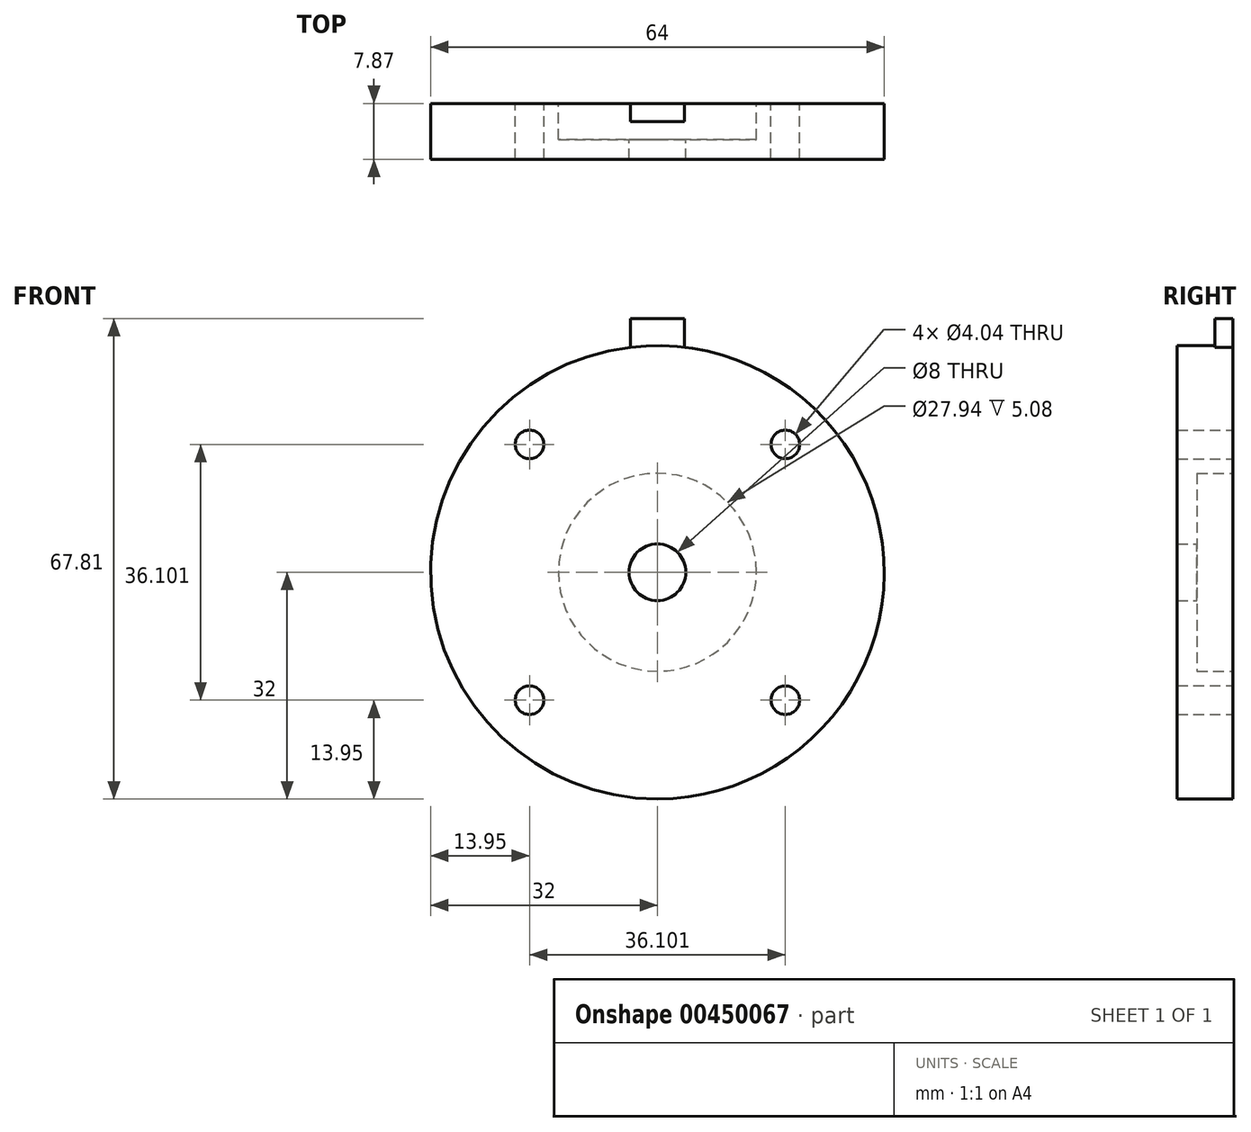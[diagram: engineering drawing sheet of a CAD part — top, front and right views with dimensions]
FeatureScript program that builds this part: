
annotation { "Feature Type Name" : "Feature", "Feature Type Description" : "" }
export const myFeature = defineFeature(function(context is Context, id is Id, definition is map)
    precondition{}
    {
        {
            var Q0;
            Q0=qCreatedBy(makeId("Front.planeOp"),FACE);
            var sketch = newSketch(context, id + "F0", { "sketchPlane" : qUnion([Q0])});
            skCircle(sketch, "E0", {"center": v(0, 0) * mm, "radius": 32 * mm});
            skCircle(sketch, "E1", {"center": v(0, 0) * mm, "radius": 4 * mm});
            skLineSegment(sketch, "E2", {"start": v(-22.63, 22.63) * mm, "end": v(-19.48, 19.48) * mm, "construction": true});
            skLineSegment(sketch, "E3", {"start": v(22.63, 22.63) * mm, "end": v(19.48, 19.48) * mm, "construction": true});
            skCircle(sketch, "E4", {"center": v(-18.05, 18.05) * mm, "radius": 2.02 * mm});
            skArc(sketch, "E5", {"start": v(19.48, 19.48) * mm, "mid": v(16.62, 19.48) * mm, "end": v(16.62, 16.62) * mm});
            skArc(sketch, "E6", {"start": v(16.62, 16.62) * mm, "mid": v(19.48, 16.62) * mm, "end": v(19.48, 19.48) * mm});
            skArc(sketch, "E7", {"start": v(16.62, -16.62) * mm, "mid": v(16.62, -19.48) * mm, "end": v(19.48, -19.48) * mm});
            skArc(sketch, "E8", {"start": v(19.48, -19.48) * mm, "mid": v(19.48, -16.62) * mm, "end": v(16.62, -16.62) * mm});
            skLineSegment(sketch, "E9", {"start": v(-16.62, -16.62) * mm, "end": v(-16.62, -16.62) * mm});
            skArc(sketch, "E10", {"start": v(-19.48, -19.48) * mm, "mid": v(-16.62, -19.48) * mm, "end": v(-16.62, -16.62) * mm});
            skArc(sketch, "E11", {"start": v(-16.62, -16.62) * mm, "mid": v(-19.48, -16.62) * mm, "end": v(-19.48, -19.48) * mm});
            skLineSegment(sketch, "E12", {"start": v(19.48, -19.48) * mm, "end": v(22.63, -22.63) * mm, "construction": true});
            skLineSegment(sketch, "E13", {"start": v(-19.48, -19.48) * mm, "end": v(-22.63, -22.63) * mm, "construction": true});
            skSolve(sketch);
        }
        {
            var Q0;
            Q0=makeQuery(id+"F0.imprint","IMPRINT",FACE,{"disambiguationData":[TD([[makeQuery(id+"F0.imprint","IMPRINT",EDGE,{"derivedFrom":sQuery(id+"F0.wireOp",EDGE,"E0")}),1.0]])]});
            extrude(context, id + "F1", {"entities" : qUnion([Q0]), "depth" : 7.87 * mm});
        }
        {
            var Q0;
            Q0=qCreatedBy(makeId("Top.planeOp"),FACE);
            cPlane(context, id + "F2", {"entities" : qUnion([Q0]), "cplaneType" : CPlaneType.OFFSET, "offset" : 32 * mm, "width" : 152.4 * mm, "height" : 152.4 * mm});
        }
        {
            var Q0;
            Q0=qCreatedBy(id+"F2.planeOp",FACE);
            var sketch = newSketch(context, id + "F3", { "sketchPlane" : qUnion([Q0])});
            skLineSegment(sketch, "E14.0", {"start": v(32, 0) * mm, "end": v(-32, 0) * mm});
            skLineSegment(sketch, "E15", {"start": v(-3.81, 0) * mm, "end": v(-3.8, -2.54) * mm});
            skLineSegment(sketch, "E16", {"start": v(-3.8, -2.54) * mm, "end": v(3.8, -2.54) * mm});
            skLineSegment(sketch, "E17", {"start": v(3.81, -2.54) * mm, "end": v(3.8, 0) * mm});
            skPoint(sketch, "E18", {"position": v(0, -2.54) * mm});
            skSolve(sketch);
        }
        {
            var Q0;
            {var subQ0=sQuery(id+"F3.wireOp",EDGE,"E15");Q0=makeQuery(id+"F3.imprint","IMPRINT",FACE,{"disambiguationData":[TD([[makeQuery(id+"F3.imprint","IMPRINT",EDGE,{"derivedFrom":subQ0}),1.0]])]});}
            var Q1;
            Q1=makeQuery(id+"F1.opExtrude","SWEPT_FACE",FACE,{"disambiguationData":[OSD([sQuery(id+"F0.wireOp",EDGE,"E0")])]});
            extrude(context, id + "F4", {"entities" : qUnion([Q0]), "operationType" : NewBodyOperationType.ADD, "depth" : 3.8 * mm, "hasSecondDirection" : true, "secondDirectionBound" : BoundingType.UP_TO_SURFACE, "secondDirectionOppositeDirection" : true, "secondDirectionBoundEntityFace" : qUnion([Q1]), "secondDirectionDepth" : 25.4 * mm});
        }
        {
            var Q0;
            Q0=makeQuery(id+"F4.boolean.opBoolean","MERGE",FACE,{"derivedFrom":[makeQuery(id+"F1.opExtrude","CAP_FACE",FACE,{"disambiguationData":[OSD([sQuery(id+"F0.wireOp",EDGE,"E0"),sQuery(id+"F0.wireOp",EDGE,"E1"),sQuery(id+"F0.wireOp",EDGE,"E4"),sQuery(id+"F0.wireOp",EDGE,"E5"),sQuery(id+"F0.wireOp",EDGE,"E6"),sQuery(id+"F0.wireOp",EDGE,"E7"),sQuery(id+"F0.wireOp",EDGE,"E8"),sQuery(id+"F0.wireOp",EDGE,"E10"),sQuery(id+"F0.wireOp",EDGE,"E11")])],"isStart":true}),makeQuery(id+"F4.opExtrude","SWEPT_FACE",FACE,{"disambiguationData":[OSD([sQuery(id+"F3.wireOp",EDGE,"E14.0")])]})]});
            var sketch = newSketch(context, id + "F5", { "sketchPlane" : qUnion([Q0])});
            skCircle(sketch, "E19", {"center": v(0, 0) * mm, "radius": 13.97 * mm});
            skSolve(sketch);
        }
        {
            var Q0;
            Q0=makeQuery(id+"F5.imprint","IMPRINT",FACE,{"disambiguationData":[TD([[makeQuery(id+"F5.imprint","IMPRINT",EDGE,{"derivedFrom":sQuery(id+"F5.wireOp",EDGE,"E19")}),1.0]])]});
            extrude(context, id + "F6", {"entities" : qUnion([Q0]), "operationType" : NewBodyOperationType.REMOVE, "oppositeDirection" : true, "depth" : 5.08 * mm});
        }
    });
